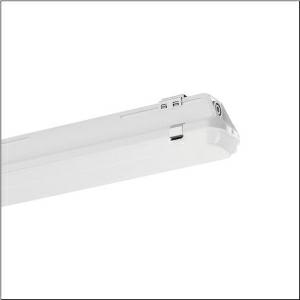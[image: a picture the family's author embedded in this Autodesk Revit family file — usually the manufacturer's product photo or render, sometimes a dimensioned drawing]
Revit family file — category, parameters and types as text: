
# Revit family: monsun_r__11_emergency_51fp20dp467l3h_369f
name_source: partatom
category: Lighting Fixtures
units: mm (PartAtom-declared; Revit-internal decimal feet)

## family parameters
Cut with Voids When Loaded = No
Host = Face
Light Source = No
Part Type = Normal
Room Calculation Point = No
Round Connector Dimension = Use Diameter
Shared = No

## types (1)
- --- (1 x LED, 910 lm, 6.2 W, 4000K)
    Apparent Load = 6 VA
    CIE Flux Codes = 45 75 93 94 100
    Color Rendering = 80
    Color Temperature = 4000K
    Default Elevation = 1800 mm
    Description = Monsun® 11 emergency, damp-proof luminaire, chain hanger, primary optical cover: enclosure, of PC, light emission: direct distribution, primary light characteristic: symmetric, installation type: suspended mounting, surface-mounted, horizontal mounting, vertical mounting, LED, rated luminous flux: 5.450lm, luminous efficacy: 173lm/W, light colour: 840, colour temperature: 4000K, control gear: DALI 2, with terminal, 5+3-pole, max. 2.5mm², mains connection: 220..240V, AC, 50/60Hz, rated input power: 35W, control gear: single battery element, battery: LiFePO4, 9Ah, luminaire housing, of glass-fibre reinforced polyester, uncoated, bright grey, incl. chain hanger, length: 1.590mm, width: 90mm, height: 88mm, clip for enclosure, of stainless steel (V2A), ceiling mounting element, of stainless steel (V2A), chain hanger, of stainless steel (V2A), protection rating (complete): IP66, insulation class (complete): insulation class I (protective earthing), certification: CE, UKCA, protection symbol: D, impact resistance: IK08, permissible operating ambient temperature: +5..+35°C, standard: EN 50419, EN 60598-2-1, EN 60598-2-22, contact your sales advisor before using the luminaires in applications with unclear chemical exposure, large temperature fluctuations or condensation-forming humidity, LABS conformity tested according to VDMA 24364:2018-05, no direct snow, no direct sun, no direct rain, for indoor or canopied outdoor use, corresponds to IFS (International Featured Standards) requirements for safety and quality in the food industry, packaging unit: 1 piece
    Height = 89 mm
    Lamp = 1 x LED
    Lamp Light Flux = 910 lm
    Lamp Power = 6.2 W
    Lamp count = 1
    Length = 1590 mm
    Luminous efficacy = 147 lm/W
    Manufacturer = Siteco
    ModVariant = No
    Model = 51FP20DP467L3H
    Mounting Place = Ceiling
    Mounting Type = Surface mounted
    Number of Poles = 1
    OnlyDefault = Yes
    Power Factor = 1
    Product Name = Monsun® 11 emergency
    Product group = damp-proof luminaire
    ProductGroupID = 301
    Protection Class = Protection class I
    Protection Degree = IP 66
    RLX_Detail_Level = 1
    RLX_Emergency_Light_Flux = 0 lm
    RLX_Emergency_Type = 0
    RLX_Emergency_Type_DB = No
    RlxData = <blob elided: 92805 chars, md5=a06fefef>
    Socket = socket
    Standby Power = 0 W
    System Light Flux = 910 lm
    System Power = 6 W
    Type Comments = : emergency light operation: 3 h
    Type Image = l_1349237.jpg
    URL = http://relux.com
    VarID = @adj_038225
    Voltage = 0 V
    Weight = 0.00 kg
    Width = 90 mm

## geometry (parser evidence)
native form markers: Blend x4, Sweep x14
no freeform markers — native parametric forms only
